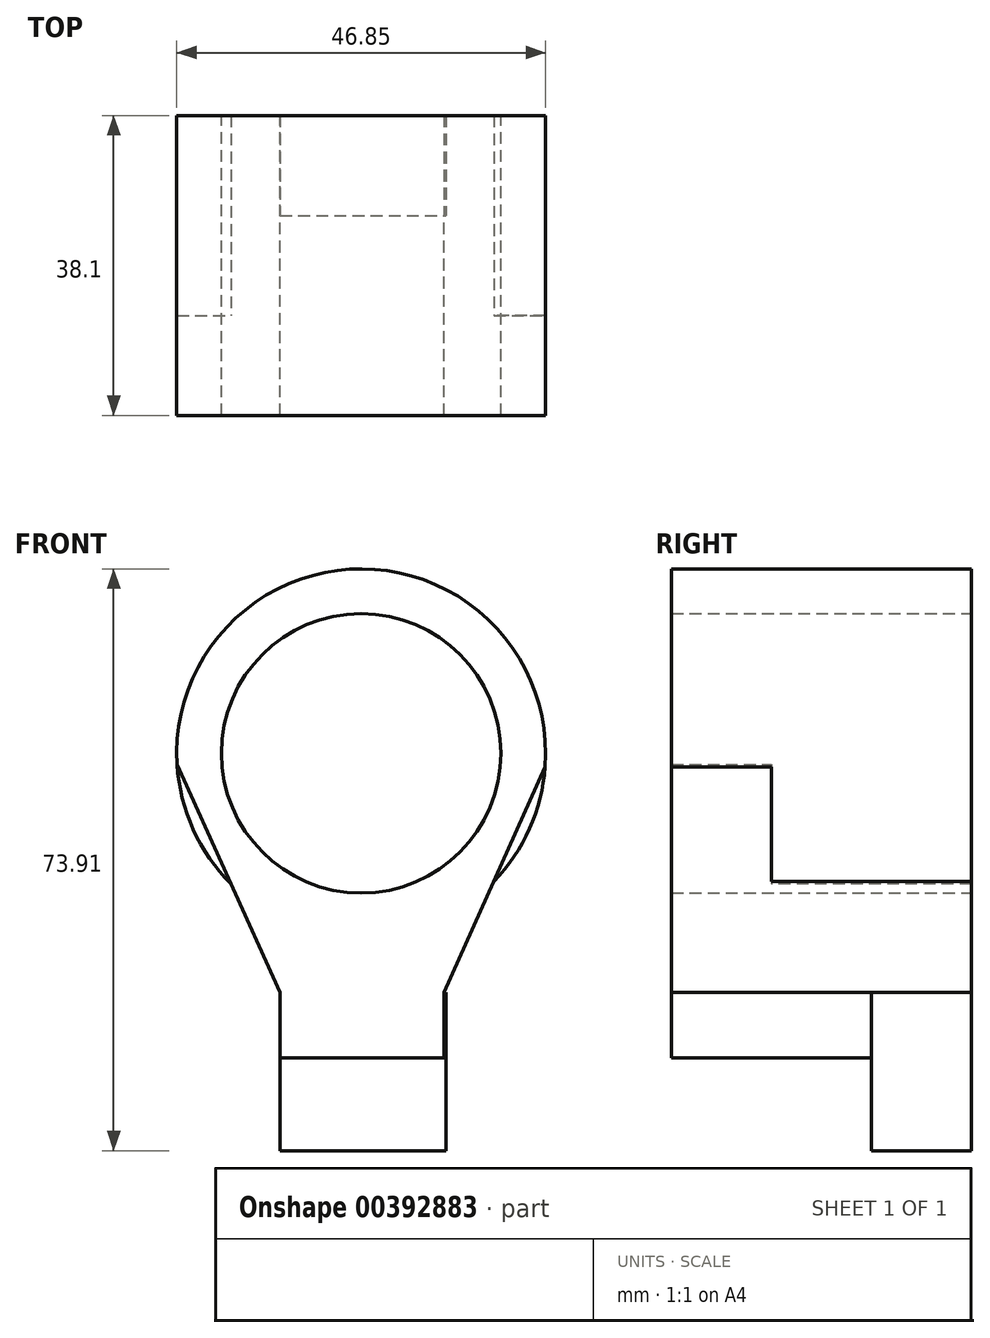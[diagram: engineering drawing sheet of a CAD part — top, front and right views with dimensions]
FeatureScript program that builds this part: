
annotation { "Feature Type Name" : "Feature", "Feature Type Description" : "" }
export const myFeature = defineFeature(function(context is Context, id is Id, definition is map)
    precondition{}
    {
        {
            var Q0;
            Q0=qCreatedBy(makeId("Front.planeOp"),FACE);
            var sketch = newSketch(context, id + "F0", { "sketchPlane" : qUnion([Q0])});
            skCircle(sketch, "E0", {"center": v(28.92, 23.65) * mm, "radius": 23.43 * mm});
            skCircle(sketch, "E1", {"center": v(28.92, 23.65) * mm, "radius": 17.75 * mm});
            skLineSegment(sketch, "E2.bottom", {"start": v(18.62, -6.74) * mm, "end": v(39.45, -6.74) * mm});
            skLineSegment(sketch, "E2.top", {"start": v(18.62, -15.07) * mm, "end": v(39.45, -15.07) * mm});
            skLineSegment(sketch, "E2.left", {"start": v(18.62, -6.74) * mm, "end": v(18.62, -15.07) * mm});
            skLineSegment(sketch, "E2.right", {"start": v(39.45, -6.74) * mm, "end": v(39.45, -15.07) * mm});
            skLineSegment(sketch, "E3.bottom", {"start": v(25.49, -15.07) * mm, "end": v(33.33, -15.07) * mm});
            skLineSegment(sketch, "E3.top", {"start": v(25.49, -26.83) * mm, "end": v(33.33, -26.83) * mm});
            skLineSegment(sketch, "E3.left", {"start": v(25.49, -15.07) * mm, "end": v(25.49, -26.83) * mm});
            skLineSegment(sketch, "E3.right", {"start": v(33.33, -15.07) * mm, "end": v(33.33, -26.83) * mm});
            skLineSegment(sketch, "E4", {"start": v(5.53, 22.2) * mm, "end": v(18.62, -6.74) * mm});
            skLineSegment(sketch, "E5", {"start": v(52.28, 21.94) * mm, "end": v(39.45, -6.74) * mm});
            skLineSegment(sketch, "E6.bottom", {"start": v(18.62, -6.74) * mm, "end": v(39.7, -6.74) * mm});
            skLineSegment(sketch, "E6.top", {"start": v(18.62, -26.83) * mm, "end": v(39.7, -26.83) * mm});
            skLineSegment(sketch, "E6.left", {"start": v(18.62, -6.74) * mm, "end": v(18.62, -26.83) * mm});
            skLineSegment(sketch, "E6.right", {"start": v(39.7, -6.74) * mm, "end": v(39.7, -26.83) * mm});
            skSolve(sketch);
        }
        {
            var Q0;
            Q0=makeQuery(id+"F0.imprint","IMPRINT",FACE,{"disambiguationData":[TD([[makeQuery(id+"F0.imprint","IMPRINT",EDGE,{"derivedFrom":sQuery(id+"F0.wireOp",EDGE,"E1")}),-1.0]])]});
            var Q1;
            {var subQ0=sQuery(id+"F0.wireOp",EDGE,"E4");var subQ1=sQuery(id+"F0.wireOp",EDGE,"E0");var subQ2=makeQuery(id+"F0.imprint","INTERSECT",VERTEX,{"disambiguationData":[OD(1.0)],"derivedFrom":[subQ1,subQ0]});Q1=makeQuery(id+"F0.imprint","IMPRINT",FACE,{"disambiguationData":[TD([[makeQuery(id+"F0.imprint","IMPRINT",EDGE,{"disambiguationData":[TD([[subQ2,-1.0]])],"derivedFrom":subQ1}),-1.0]])]});}
            var Q2;
            {var subQ1=sQuery(id+"F0.wireOp",EDGE,"E2.right");Q2=makeQuery(id+"F0.imprint","IMPRINT",FACE,{"disambiguationData":[TD([[makeQuery(id+"F0.imprint","IMPRINT",EDGE,{"derivedFrom":subQ1}),-1.0]])]});}
            var Q3;
            Q3=makeQuery(id+"F0.imprint","IMPRINT",FACE,{"disambiguationData":[TD([[makeQuery(id+"F0.imprint","IMPRINT",EDGE,{"derivedFrom":sQuery(id+"F0.wireOp",EDGE,"E3.bottom")}),-1.0]])]});
            extrude(context, id + "F1", {"entities" : qUnion([Q0, Q1, Q2, Q3]), "depth" : 12.7 * mm});
        }
        {
            var Q0;
            Q0 = qSketchRegion(id + "F0", true);
            extrude(context, id + "F2", {"entities" : qUnion([Q0]), "operationType" : NewBodyOperationType.ADD, "depth" : -12.7 * mm});
        }
        {
            var Q0;
            Q0=makeQuery(id+"F2.opExtrude","CAP_FACE",FACE,{"disambiguationData":[OSD([sQuery(id+"F0.wireOp",EDGE,"E0"),sQuery(id+"F0.wireOp",EDGE,"E1"),sQuery(id+"F0.wireOp",EDGE,"E4"),sQuery(id+"F0.wireOp",EDGE,"E5"),sQuery(id+"F0.wireOp",EDGE,"E6.bottom"),sQuery(id+"F0.wireOp",EDGE,"E6.top"),sQuery(id+"F0.wireOp",EDGE,"E6.left"),sQuery(id+"F0.wireOp",EDGE,"E6.right")])],"isStart":false});
            extrude(context, id + "F3", {"entities" : qUnion([Q0]), "operationType" : NewBodyOperationType.ADD, "depth" : 12.7 * mm});
        }
        {
            var Q0;
            {var subQ0=sQuery(id+"F0.wireOp",EDGE,"E3.right");var subQ1=sQuery(id+"F0.wireOp",EDGE,"E2.right");var subQ2=sQuery(id+"F0.wireOp",EDGE,"E5");var subQ3=sQuery(id+"F0.wireOp",EDGE,"E6.bottom");var subQ4=sQuery(id+"F0.wireOp",EDGE,"E2.top");var subQ5=sQuery(id+"F0.wireOp",EDGE,"E6.top");var subQ6=sQuery(id+"F0.wireOp",EDGE,"E6.right");Q0=makeQuery(id+"F2.boolean.opBoolean","SPLIT",FACE,{"disambiguationData":[TD([makeQuery(id+"F1.opExtrude","SWEPT_FACE",FACE,{"disambiguationData":[OSD([subQ4]),TDD([makeQuery(id+"F0.imprint","IMPRINT",EDGE,{"disambiguationData":[TD([[makeQuery(id+"F0.imprint","INTERSECT",VERTEX,{"derivedFrom":[subQ4,subQ1]}),1.0]])],"derivedFrom":subQ4})])]}),makeQuery(id+"F1.opExtrude","SWEPT_FACE",FACE,{"disambiguationData":[OSD([subQ1])]}),makeQuery(id+"F1.opExtrude","SWEPT_FACE",FACE,{"disambiguationData":[OSD([subQ0])]}),makeQuery(id+"F1.opExtrude","SWEPT_FACE",FACE,{"disambiguationData":[OSD([subQ2])]}),makeQuery(id+"F1.opExtrude","SWEPT_FACE",FACE,{"disambiguationData":[OSD([subQ5])]}),makeQuery(id+"F2.opExtrude","SWEPT_FACE",FACE,{"disambiguationData":[OSD([subQ2])]}),makeQuery(id+"F2.opExtrude","SWEPT_FACE",FACE,{"disambiguationData":[OSD([subQ3])]}),makeQuery(id+"F2.opExtrude","SWEPT_FACE",FACE,{"disambiguationData":[OSD([subQ5])]}),makeQuery(id+"F2.opExtrude","SWEPT_FACE",FACE,{"disambiguationData":[OSD([subQ6])]})])],"derivedFrom":makeQuery(id+"F2.opExtrude","CAP_FACE",FACE,{"disambiguationData":[OSD([sQuery(id+"F0.wireOp",EDGE,"E0"),sQuery(id+"F0.wireOp",EDGE,"E1"),sQuery(id+"F0.wireOp",EDGE,"E4"),subQ2,subQ3,subQ5,sQuery(id+"F0.wireOp",EDGE,"E6.left"),subQ6])],"isStart":true})});}
            var Q1;
            {var subQ0=sQuery(id+"F0.wireOp",EDGE,"E6.top");var subQ1=sQuery(id+"F0.wireOp",EDGE,"E6.left");var subQ2=sQuery(id+"F0.wireOp",EDGE,"E3.left");var subQ3=sQuery(id+"F0.wireOp",EDGE,"E2.top");Q1=makeQuery(id+"F2.boolean.opBoolean","SPLIT",FACE,{"disambiguationData":[TD([makeQuery(id+"F1.opExtrude","SWEPT_FACE",FACE,{"disambiguationData":[OSD([subQ3]),TDD([makeQuery(id+"F0.imprint","IMPRINT",EDGE,{"disambiguationData":[TD([[makeQuery(id+"F0.imprint","INTERSECT",VERTEX,{"derivedFrom":[subQ3,subQ1]}),-1.0]])],"derivedFrom":subQ3})])]}),makeQuery(id+"F1.opExtrude","SWEPT_FACE",FACE,{"disambiguationData":[OSD([subQ2])]}),makeQuery(id+"F1.opExtrude","SWEPT_FACE",FACE,{"disambiguationData":[OSD([subQ0])]}),makeQuery(id+"F1.opExtrude","SWEPT_FACE",FACE,{"disambiguationData":[OSD([subQ1])]}),makeQuery(id+"F2.opExtrude","SWEPT_FACE",FACE,{"disambiguationData":[OSD([subQ0])]}),makeQuery(id+"F2.opExtrude","SWEPT_FACE",FACE,{"disambiguationData":[OSD([subQ1])]})])],"derivedFrom":makeQuery(id+"F2.opExtrude","CAP_FACE",FACE,{"disambiguationData":[OSD([sQuery(id+"F0.wireOp",EDGE,"E0"),sQuery(id+"F0.wireOp",EDGE,"E1"),sQuery(id+"F0.wireOp",EDGE,"E4"),sQuery(id+"F0.wireOp",EDGE,"E5"),sQuery(id+"F0.wireOp",EDGE,"E6.bottom"),subQ0,subQ1,sQuery(id+"F0.wireOp",EDGE,"E6.right")])],"isStart":true})});}
            extrude(context, id + "F4", {"entities" : qUnion([Q0, Q1]), "operationType" : NewBodyOperationType.ADD, "depth" : -12.7 * mm});
        }
        {
            var Q0;
            {var subQ0=sQuery(id+"F0.wireOp",EDGE,"E3.right");var subQ1=sQuery(id+"F0.wireOp",EDGE,"E2.right");var subQ2=sQuery(id+"F0.wireOp",EDGE,"E5");var subQ3=sQuery(id+"F0.wireOp",EDGE,"E6.bottom");var subQ4=sQuery(id+"F0.wireOp",EDGE,"E2.top");var subQ5=sQuery(id+"F0.wireOp",EDGE,"E6.top");var subQ6=sQuery(id+"F0.wireOp",EDGE,"E6.right");Q0=makeQuery(id+"F2.boolean.opBoolean","SPLIT",FACE,{"disambiguationData":[TD([makeQuery(id+"F1.opExtrude","SWEPT_FACE",FACE,{"disambiguationData":[OSD([subQ4]),TDD([makeQuery(id+"F0.imprint","IMPRINT",EDGE,{"disambiguationData":[TD([[makeQuery(id+"F0.imprint","INTERSECT",VERTEX,{"derivedFrom":[subQ4,subQ1]}),1.0]])],"derivedFrom":subQ4})])]}),makeQuery(id+"F1.opExtrude","SWEPT_FACE",FACE,{"disambiguationData":[OSD([subQ1])]}),makeQuery(id+"F1.opExtrude","SWEPT_FACE",FACE,{"disambiguationData":[OSD([subQ0])]}),makeQuery(id+"F1.opExtrude","SWEPT_FACE",FACE,{"disambiguationData":[OSD([subQ2])]}),makeQuery(id+"F1.opExtrude","SWEPT_FACE",FACE,{"disambiguationData":[OSD([subQ5])]}),makeQuery(id+"F2.opExtrude","SWEPT_FACE",FACE,{"disambiguationData":[OSD([subQ2])]}),makeQuery(id+"F2.opExtrude","SWEPT_FACE",FACE,{"disambiguationData":[OSD([subQ3])]}),makeQuery(id+"F2.opExtrude","SWEPT_FACE",FACE,{"disambiguationData":[OSD([subQ5])]}),makeQuery(id+"F2.opExtrude","SWEPT_FACE",FACE,{"disambiguationData":[OSD([subQ6])]})])],"derivedFrom":makeQuery(id+"F2.opExtrude","CAP_FACE",FACE,{"disambiguationData":[OSD([sQuery(id+"F0.wireOp",EDGE,"E0"),sQuery(id+"F0.wireOp",EDGE,"E1"),sQuery(id+"F0.wireOp",EDGE,"E4"),subQ2,subQ3,subQ5,sQuery(id+"F0.wireOp",EDGE,"E6.left"),subQ6])],"isStart":true})});}
            var Q1;
            {var subQ0=sQuery(id+"F0.wireOp",EDGE,"E6.top");var subQ1=sQuery(id+"F0.wireOp",EDGE,"E6.left");var subQ2=sQuery(id+"F0.wireOp",EDGE,"E3.left");var subQ3=sQuery(id+"F0.wireOp",EDGE,"E2.top");Q1=makeQuery(id+"F2.boolean.opBoolean","SPLIT",FACE,{"disambiguationData":[TD([makeQuery(id+"F1.opExtrude","SWEPT_FACE",FACE,{"disambiguationData":[OSD([subQ3]),TDD([makeQuery(id+"F0.imprint","IMPRINT",EDGE,{"disambiguationData":[TD([[makeQuery(id+"F0.imprint","INTERSECT",VERTEX,{"derivedFrom":[subQ3,subQ1]}),-1.0]])],"derivedFrom":subQ3})])]}),makeQuery(id+"F1.opExtrude","SWEPT_FACE",FACE,{"disambiguationData":[OSD([subQ2])]}),makeQuery(id+"F1.opExtrude","SWEPT_FACE",FACE,{"disambiguationData":[OSD([subQ0])]}),makeQuery(id+"F1.opExtrude","SWEPT_FACE",FACE,{"disambiguationData":[OSD([subQ1])]}),makeQuery(id+"F2.opExtrude","SWEPT_FACE",FACE,{"disambiguationData":[OSD([subQ0])]}),makeQuery(id+"F2.opExtrude","SWEPT_FACE",FACE,{"disambiguationData":[OSD([subQ1])]})])],"derivedFrom":makeQuery(id+"F2.opExtrude","CAP_FACE",FACE,{"disambiguationData":[OSD([sQuery(id+"F0.wireOp",EDGE,"E0"),sQuery(id+"F0.wireOp",EDGE,"E1"),sQuery(id+"F0.wireOp",EDGE,"E4"),sQuery(id+"F0.wireOp",EDGE,"E5"),sQuery(id+"F0.wireOp",EDGE,"E6.bottom"),subQ0,subQ1,sQuery(id+"F0.wireOp",EDGE,"E6.right")])],"isStart":true})});}
            extrude(context, id + "F5", {"entities" : qUnion([Q0, Q1]), "operationType" : NewBodyOperationType.REMOVE, "oppositeDirection" : true, "depth" : -12.7 * mm, "hasSecondDirection" : true, "secondDirectionOppositeDirection" : false, "secondDirectionDepth" : -12.7 * mm});
        }
    });
